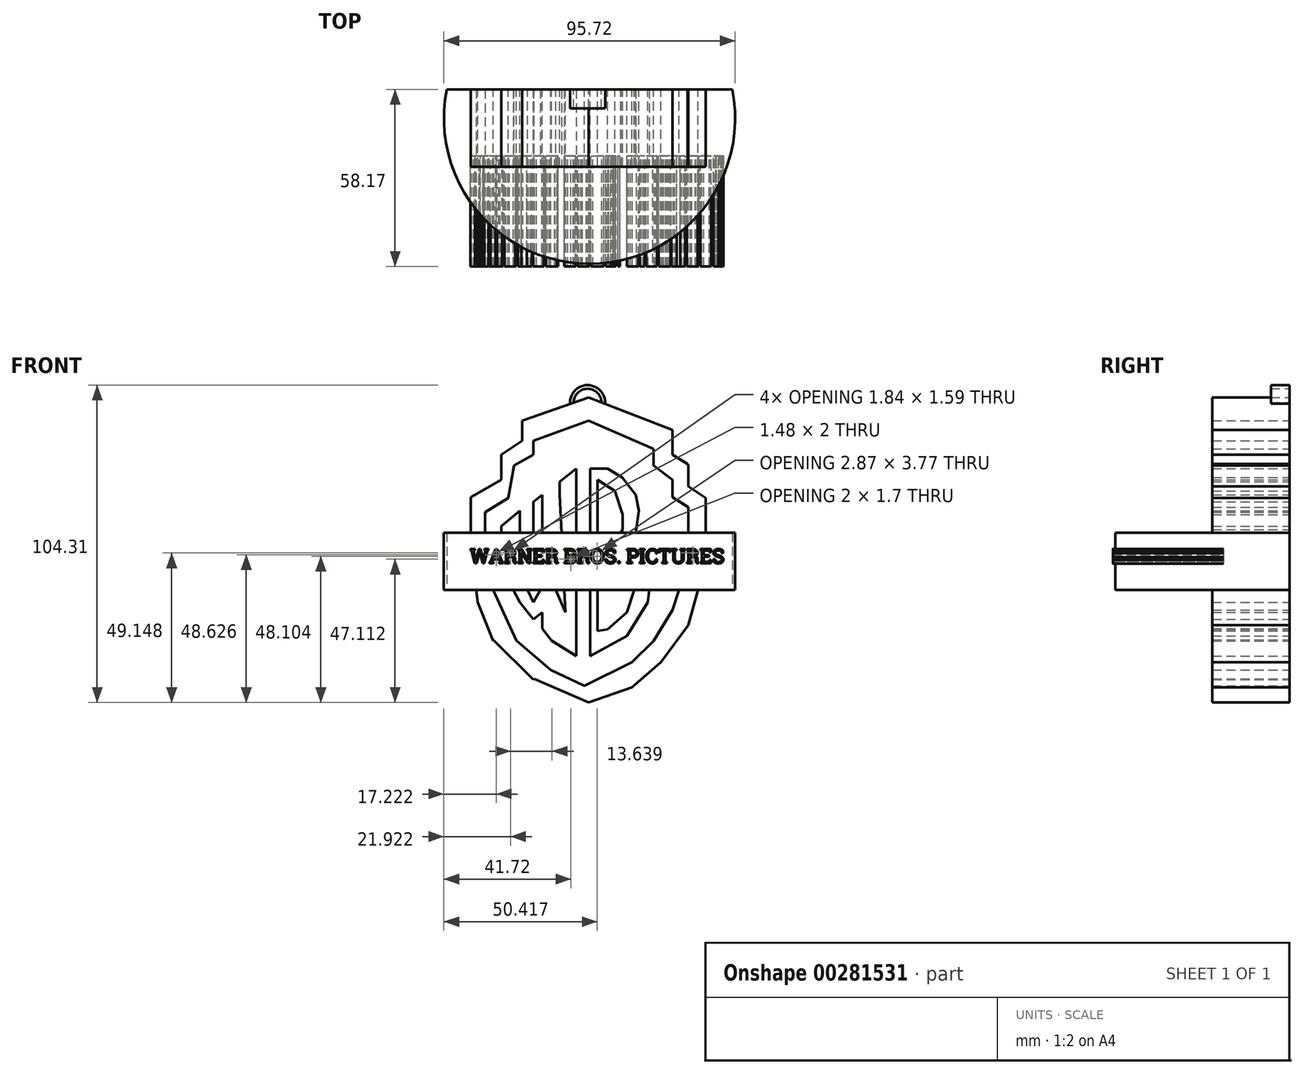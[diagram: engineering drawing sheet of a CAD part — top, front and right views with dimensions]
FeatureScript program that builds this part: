
annotation { "Feature Type Name" : "Feature", "Feature Type Description" : "" }
export const myFeature = defineFeature(function(context is Context, id is Id, definition is map)
    precondition{}
    {
        {
            var Q0;
            Q0=qCreatedBy(makeId("Front.planeOp"),FACE);
            var sketch = newSketch(context, id + "F0", { "sketchPlane" : qUnion([Q0])});
            skLineSegment(sketch, "E0", {"start": v(-31.57, 21) * mm, "end": v(-31.57, 14.04) * mm});
            skLineSegment(sketch, "E1", {"start": v(-31.57, 14.04) * mm, "end": v(-29.37, 3.28) * mm});
            skLineSegment(sketch, "E2", {"start": v(-29.37, 3.28) * mm, "end": v(-25.56, -4) * mm});
            skLineSegment(sketch, "E3", {"start": v(-25.56, -4) * mm, "end": v(-21.1, -9.61) * mm});
            skLineSegment(sketch, "E4", {"start": v(-21.1, -9.61) * mm, "end": v(-18.2, -7.3) * mm});
            skLineSegment(sketch, "E5", {"start": v(-18.2, -7.3) * mm, "end": v(-18.2, -12.73) * mm});
            skLineSegment(sketch, "E6", {"start": v(-18.2, -12.73) * mm, "end": v(-15.13, -16.59) * mm});
            skLineSegment(sketch, "E7", {"start": v(-15.13, -16.59) * mm, "end": v(-6.92, -21.74) * mm});
            skLineSegment(sketch, "E8", {"start": v(-6.92, -21.74) * mm, "end": v(-6.92, 35.57) * mm});
            skLineSegment(sketch, "E9", {"start": v(-6.92, 35.57) * mm, "end": v(-12.38, 31.25) * mm});
            skLineSegment(sketch, "E10", {"start": v(-12.38, 31.25) * mm, "end": v(-10.58, -7.3) * mm});
            skLineSegment(sketch, "E11", {"start": v(-10.58, -7.3) * mm, "end": v(-15.13, 3.28) * mm});
            skLineSegment(sketch, "E12", {"start": v(-15.13, 3.28) * mm, "end": v(-18.2, 18.82) * mm});
            skLineSegment(sketch, "E13", {"start": v(-18.2, 18.82) * mm, "end": v(-18.2, 26.1) * mm});
            skLineSegment(sketch, "E14", {"start": v(-18.2, 26.1) * mm, "end": v(-21.1, 23.8) * mm});
            skLineSegment(sketch, "E15", {"start": v(-21.1, 23.8) * mm, "end": v(-21.1, 18.82) * mm});
            skLineSegment(sketch, "E16", {"start": v(-21.1, 18.82) * mm, "end": v(-18.2, 3.28) * mm});
            skLineSegment(sketch, "E17", {"start": v(-18.2, 3.28) * mm, "end": v(-18.2, 0.92) * mm});
            skLineSegment(sketch, "E18", {"start": v(-21.1, -4.1) * mm, "end": v(-24.53, 3.28) * mm});
            skLineSegment(sketch, "E19", {"start": v(-24.53, 3.28) * mm, "end": v(-25.56, 14.04) * mm});
            skLineSegment(sketch, "E20", {"start": v(-25.56, 14.04) * mm, "end": v(-25.56, 26.1) * mm});
            skLineSegment(sketch, "E21", {"start": v(-25.56, 26.1) * mm, "end": v(-31.57, 21) * mm});
            skLineSegment(sketch, "E22", {"start": v(-18.2, 26.1) * mm, "end": v(-18.2, 31.25) * mm});
            skLineSegment(sketch, "E23", {"start": v(-18.2, 31.25) * mm, "end": v(-21.1, 28.94) * mm});
            skLineSegment(sketch, "E24", {"start": v(-21.1, 28.94) * mm, "end": v(-21.1, 23.8) * mm});
            skLineSegment(sketch, "E25", {"start": v(-12.38, 31.25) * mm, "end": v(-12.38, 35.57) * mm});
            skLineSegment(sketch, "E26", {"start": v(-12.38, 35.57) * mm, "end": v(-6.92, 39.9) * mm});
            skLineSegment(sketch, "E27", {"start": v(-6.92, 39.9) * mm, "end": v(-6.92, 35.57) * mm});
            skLineSegment(sketch, "E28", {"start": v(-2.43, -21.74) * mm, "end": v(-2.43, 39.9) * mm});
            skLineSegment(sketch, "E29", {"start": v(-2.43, 39.9) * mm, "end": v(3.37, 39.9) * mm});
            skLineSegment(sketch, "E30", {"start": v(3.37, 39.9) * mm, "end": v(8.13, 36.9) * mm});
            skLineSegment(sketch, "E31", {"start": v(8.13, 36.9) * mm, "end": v(12.62, 31.25) * mm});
            skLineSegment(sketch, "E32", {"start": v(12.62, 31.25) * mm, "end": v(13.63, 26.1) * mm});
            skLineSegment(sketch, "E33", {"start": v(13.63, 26.1) * mm, "end": v(12.62, 18.82) * mm});
            skLineSegment(sketch, "E34", {"start": v(12.62, 18.82) * mm, "end": v(9.62, 14.04) * mm});
            skLineSegment(sketch, "E35", {"start": v(9.62, 14.04) * mm, "end": v(13.63, 11.52) * mm});
            skLineSegment(sketch, "E36", {"start": v(13.63, 11.52) * mm, "end": v(16.5, 7.9) * mm});
            skLineSegment(sketch, "E37", {"start": v(16.5, 7.9) * mm, "end": v(17.42, 3.28) * mm});
            skLineSegment(sketch, "E38", {"start": v(17.42, 3.28) * mm, "end": v(16.5, -4.1) * mm});
            skLineSegment(sketch, "E39", {"start": v(16.5, -4.1) * mm, "end": v(14.5, -7.3) * mm});
            skLineSegment(sketch, "E40", {"start": v(14.5, -7.3) * mm, "end": v(9.62, -15.06) * mm});
            skLineSegment(sketch, "E41", {"start": v(9.62, -15.06) * mm, "end": v(-2.43, -21.74) * mm});
            skLineSegment(sketch, "E42", {"start": v(0, -13.51) * mm, "end": v(0, 4.3) * mm});
            skLineSegment(sketch, "E43", {"start": v(0, 4.3) * mm, "end": v(3.37, 7.66) * mm});
            skLineSegment(sketch, "E44", {"start": v(3.37, 7.66) * mm, "end": v(7.49, 9.83) * mm});
            skLineSegment(sketch, "E45", {"start": v(7.49, 9.83) * mm, "end": v(12.03, 7.66) * mm});
            skLineSegment(sketch, "E46", {"start": v(12.03, 7.66) * mm, "end": v(12.03, 0) * mm});
            skLineSegment(sketch, "E47", {"start": v(12.03, 0) * mm, "end": v(9.63, -7.3) * mm});
            skLineSegment(sketch, "E48", {"start": v(9.63, -7.3) * mm, "end": v(3.37, -12.98) * mm});
            skLineSegment(sketch, "E49", {"start": v(3.37, -12.98) * mm, "end": v(0, -13.51) * mm});
            skLineSegment(sketch, "E50", {"start": v(0, 9.83) * mm, "end": v(5.75, 15.74) * mm});
            skPoint(sketch, "E50.endSnap0", {"position": v(5.75, 38.4) * mm});
            skLineSegment(sketch, "E51", {"start": v(5.75, 15.74) * mm, "end": v(8.29, 19.78) * mm});
            skLineSegment(sketch, "E52", {"start": v(8.29, 19.78) * mm, "end": v(8.29, 24.78) * mm});
            skLineSegment(sketch, "E53", {"start": v(8.29, 24.78) * mm, "end": v(5.75, 32.55) * mm});
            skLineSegment(sketch, "E54", {"start": v(5.75, 32.55) * mm, "end": v(3.37, 34.05) * mm});
            skLineSegment(sketch, "E55", {"start": v(3.37, 34.05) * mm, "end": v(0, 36.16) * mm});
            skLineSegment(sketch, "E56", {"start": v(0, 36.16) * mm, "end": v(0, 9.83) * mm});
            skLineSegment(sketch, "E57", {"start": v(-15.13, -16.59) * mm, "end": v(-6.92, -13.51) * mm});
            skLineSegment(sketch, "E58", {"start": v(-18.2, -12.73) * mm, "end": v(-10.58, -7.3) * mm});
            skLineSegment(sketch, "E59", {"start": v(-15.13, 3.28) * mm, "end": v(-18.2, 3.28) * mm});
            skLineSegment(sketch, "E60", {"start": v(-21.1, 18.82) * mm, "end": v(-18.2, 18.82) * mm});
            skLineSegment(sketch, "E61", {"start": v(-29.32, 30.24) * mm, "end": v(-36.93, 25.5) * mm});
            skLineSegment(sketch, "E62", {"start": v(-36.93, 25.97) * mm, "end": v(-36.93, 16.94) * mm});
            skLineSegment(sketch, "E63", {"start": v(-36.93, 16.94) * mm, "end": v(-34.31, 0) * mm});
            skLineSegment(sketch, "E64", {"start": v(-34.31, 0) * mm, "end": v(-26.7, -16.57) * mm});
            skLineSegment(sketch, "E65", {"start": v(-26.7, -16.57) * mm, "end": v(-15.3, -26.3) * mm});
            skLineSegment(sketch, "E66", {"start": v(-15.3, -26.3) * mm, "end": v(-4.37, -31.54) * mm});
            skLineSegment(sketch, "E67", {"start": v(-4.37, -31.54) * mm, "end": v(11.31, -23.7) * mm});
            skLineSegment(sketch, "E68", {"start": v(11.31, -23.7) * mm, "end": v(18.44, -16.8) * mm});
            skLineSegment(sketch, "E69", {"start": v(18.44, -16.8) * mm, "end": v(24.62, -6.59) * mm});
            skLineSegment(sketch, "E70", {"start": v(24.62, -6.59) * mm, "end": v(29.84, 9.57) * mm});
            skLineSegment(sketch, "E71", {"start": v(29.84, 9.57) * mm, "end": v(29.84, 21) * mm});
            skLineSegment(sketch, "E72", {"start": v(29.84, 21) * mm, "end": v(29.84, 27.16) * mm});
            skLineSegment(sketch, "E73", {"start": v(29.84, 27.16) * mm, "end": v(24.62, 30.48) * mm});
            skLineSegment(sketch, "E74", {"start": v(24.62, 30.48) * mm, "end": v(24.62, 36.18) * mm});
            skLineSegment(sketch, "E75", {"start": v(24.62, 36.18) * mm, "end": v(18.44, 40.94) * mm});
            skLineSegment(sketch, "E76", {"start": v(18.44, 40.94) * mm, "end": v(18.44, 46.4) * mm});
            skLineSegment(sketch, "E77", {"start": v(18.44, 46.4) * mm, "end": v(-2.95, 55.67) * mm});
            skLineSegment(sketch, "E78", {"start": v(-2.95, 55.67) * mm, "end": v(-21.1, 49.02) * mm});
            skLineSegment(sketch, "E79", {"start": v(-21.1, 49.02) * mm, "end": v(-21.1, 44.5) * mm});
            skLineSegment(sketch, "E80", {"start": v(-21.1, 44.5) * mm, "end": v(-27.42, 40.94) * mm});
            skLineSegment(sketch, "E81", {"start": v(-27.42, 40.94) * mm, "end": v(-29.32, 30.24) * mm});
            skLineSegment(sketch, "E82", {"start": v(-2.95, 63.27) * mm, "end": v(-24.8, 55.67) * mm});
            skLineSegment(sketch, "E83", {"start": v(-24.8, 55.67) * mm, "end": v(-24.8, 49.02) * mm});
            skLineSegment(sketch, "E84", {"start": v(-24.8, 49.02) * mm, "end": v(-31.57, 44.5) * mm});
            skLineSegment(sketch, "E85", {"start": v(-31.57, 44.5) * mm, "end": v(-31.57, 36.18) * mm});
            skLineSegment(sketch, "E86", {"start": v(-31.57, 36.18) * mm, "end": v(-41.68, 30.48) * mm});
            skLineSegment(sketch, "E87", {"start": v(-41.68, 30.48) * mm, "end": v(-41.68, 14.04) * mm});
            skLineSegment(sketch, "E88", {"start": v(-41.92, 13.85) * mm, "end": v(-39.3, -4.1) * mm});
            skLineSegment(sketch, "E89", {"start": v(-39.3, -4.1) * mm, "end": v(-34.31, -16.8) * mm});
            skLineSegment(sketch, "E90", {"start": v(-34.31, -16.33) * mm, "end": v(-21.1, -29.4) * mm});
            skLineSegment(sketch, "E91", {"start": v(-20.77, -29.16) * mm, "end": v(-2.95, -37) * mm});
            skLineSegment(sketch, "E92", {"start": v(-2.95, -37) * mm, "end": v(11.31, -32.01) * mm});
            skLineSegment(sketch, "E93", {"start": v(11.31, -32.01) * mm, "end": v(20.82, -23.7) * mm});
            skLineSegment(sketch, "E94", {"start": v(20.82, -23.7) * mm, "end": v(29.84, -11.58) * mm});
            skLineSegment(sketch, "E95", {"start": v(29.84, -11.58) * mm, "end": v(35.07, 7.67) * mm});
            skLineSegment(sketch, "E96", {"start": v(35.55, 6.96) * mm, "end": v(35.55, 21) * mm});
            skLineSegment(sketch, "E97", {"start": v(35.55, 21) * mm, "end": v(35.55, 30.24) * mm});
            skLineSegment(sketch, "E98", {"start": v(35.55, 30.24) * mm, "end": v(29.84, 34.05) * mm});
            skLineSegment(sketch, "E99", {"start": v(29.84, 34.05) * mm, "end": v(29.84, 40.94) * mm});
            skLineSegment(sketch, "E100", {"start": v(29.6, 41.41) * mm, "end": v(24.62, 44.5) * mm});
            skLineSegment(sketch, "E101", {"start": v(24.62, 44.5) * mm, "end": v(24.62, 52.58) * mm});
            skLineSegment(sketch, "E102", {"start": v(24.62, 52.58) * mm, "end": v(-2.95, 63.27) * mm});
            skLineSegment(sketch, "E103", {"start": v(-21.1, 44.5) * mm, "end": v(-24.8, 49.02) * mm});
            skLineSegment(sketch, "E104", {"start": v(-27.42, 40.94) * mm, "end": v(-31.57, 44.5) * mm});
            skLineSegment(sketch, "E105", {"start": v(-29.32, 30.24) * mm, "end": v(-31.57, 36.18) * mm});
            skLineSegment(sketch, "E106", {"start": v(-36.93, 25.97) * mm, "end": v(-41.68, 30.48) * mm});
            skLineSegment(sketch, "E107", {"start": v(-36.93, 16.94) * mm, "end": v(-41.68, 14.04) * mm});
            skLineSegment(sketch, "E108", {"start": v(-34.31, 0) * mm, "end": v(-39.3, -4.1) * mm});
            skLineSegment(sketch, "E109", {"start": v(-26.7, -16.57) * mm, "end": v(-34.31, -16.33) * mm});
            skLineSegment(sketch, "E110", {"start": v(-15.3, -26.3) * mm, "end": v(-20.77, -29.16) * mm});
            skLineSegment(sketch, "E111", {"start": v(-4.37, -31.54) * mm, "end": v(-2.95, -37) * mm});
            skLineSegment(sketch, "E112", {"start": v(11.31, -23.7) * mm, "end": v(11.31, -32.01) * mm});
            skLineSegment(sketch, "E113", {"start": v(18.44, -16.8) * mm, "end": v(20.82, -23.7) * mm});
            skLineSegment(sketch, "E114", {"start": v(29.84, -11.58) * mm, "end": v(24.62, -6.59) * mm});
            skLineSegment(sketch, "E115", {"start": v(35.55, 6.96) * mm, "end": v(29.84, 9.57) * mm});
            skLineSegment(sketch, "E116", {"start": v(35.55, 21) * mm, "end": v(29.84, 21) * mm});
            skLineSegment(sketch, "E117", {"start": v(29.84, 27.16) * mm, "end": v(35.55, 30.24) * mm});
            skLineSegment(sketch, "E118", {"start": v(29.84, 34.05) * mm, "end": v(24.62, 30.48) * mm});
            skLineSegment(sketch, "E119", {"start": v(29.84, 40.94) * mm, "end": v(24.62, 36.18) * mm});
            skLineSegment(sketch, "E120", {"start": v(24.62, 44.5) * mm, "end": v(18.44, 40.94) * mm});
            skLineSegment(sketch, "E121", {"start": v(18.44, 46.4) * mm, "end": v(24.62, 52.58) * mm});
            skLineSegment(sketch, "E122", {"start": v(-2.95, 55.67) * mm, "end": v(-2.95, 63.27) * mm});
            skLineSegment(sketch, "E123", {"start": v(-34.31, -16.33) * mm, "end": v(-15.3, -26.3) * mm});
            skLineSegment(sketch, "E124", {"start": v(-26.7, -16.57) * mm, "end": v(-20.77, -29.16) * mm});
            skLineSegment(sketch, "E125", {"start": v(-39.3, -4.1) * mm, "end": v(-26.7, -16.57) * mm});
            skLineSegment(sketch, "E126", {"start": v(-34.31, 0) * mm, "end": v(-34.31, -16.33) * mm});
            skLineSegment(sketch, "E127", {"start": v(-41.68, 14.04) * mm, "end": v(-34.31, 0) * mm});
            skLineSegment(sketch, "E128", {"start": v(-36.93, 16.94) * mm, "end": v(-39.3, -4.1) * mm});
            skLineSegment(sketch, "E129", {"start": v(29.84, 40.94) * mm, "end": v(18.44, 40.94) * mm});
            skLineSegment(sketch, "E130", {"start": v(24.62, 36.18) * mm, "end": v(24.62, 44.5) * mm});
            skLineSegment(sketch, "E131", {"start": v(9.62, 14.04) * mm, "end": v(5.75, 15.74) * mm});
            skLineSegment(sketch, "E132", {"start": v(8.29, 19.78) * mm, "end": v(12.62, 18.82) * mm});
            skLineSegment(sketch, "E133", {"start": v(13.63, 26.1) * mm, "end": v(8.29, 24.78) * mm});
            skLineSegment(sketch, "E134", {"start": v(5.75, 32.55) * mm, "end": v(12.62, 31.25) * mm});
            skLineSegment(sketch, "E135", {"start": v(3.37, 34.05) * mm, "end": v(8.13, 36.9) * mm});
            skLineSegment(sketch, "E136", {"start": v(3.37, 39.9) * mm, "end": v(0, 36.16) * mm});
            skLineSegment(sketch, "E137", {"start": v(-2.43, 39.9) * mm, "end": v(0, 36.16) * mm});
            skLineSegment(sketch, "E138", {"start": v(0, 4.3) * mm, "end": v(0, 9.83) * mm});
            skLineSegment(sketch, "E139", {"start": v(3.37, 7.66) * mm, "end": v(5.75, 15.74) * mm});
            skLineSegment(sketch, "E140", {"start": v(7.49, 9.83) * mm, "end": v(9.62, 14.04) * mm});
            skLineSegment(sketch, "E141", {"start": v(12.03, 7.66) * mm, "end": v(13.63, 11.52) * mm});
            skLineSegment(sketch, "E142", {"start": v(16.5, 7.9) * mm, "end": v(12.03, 0) * mm});
            skLineSegment(sketch, "E143", {"start": v(17.42, 3.28) * mm, "end": v(9.63, -7.3) * mm});
            skLineSegment(sketch, "E144", {"start": v(16.5, -4.1) * mm, "end": v(9.63, -7.3) * mm});
            skLineSegment(sketch, "E145", {"start": v(14.5, -7.3) * mm, "end": v(9.63, -7.3) * mm});
            skLineSegment(sketch, "E146", {"start": v(3.37, -12.98) * mm, "end": v(9.62, -15.06) * mm});
            skLineSegment(sketch, "E147", {"start": v(0, -13.51) * mm, "end": v(-2.43, -21.74) * mm});
            skLineSegment(sketch, "E148", {"start": v(-21.1, -4.1) * mm, "end": v(-21.1, -9.61) * mm});
            skLineSegment(sketch, "E149", {"start": v(-18.2, -7.3) * mm, "end": v(-18.2, 0.92) * mm});
            skLineSegment(sketch, "E150", {"start": v(-24.53, 3.28) * mm, "end": v(-25.56, -4) * mm});
            skLineSegment(sketch, "E151", {"start": v(-24.53, 3.28) * mm, "end": v(-29.37, 3.28) * mm});
            skLineSegment(sketch, "E152", {"start": v(-31.57, 14.04) * mm, "end": v(-25.56, 14.04) * mm});
            skLineSegment(sketch, "E153", {"start": v(-34.31, -16.8) * mm, "end": v(-34.31, -16.33) * mm});
            skLineSegment(sketch, "E154", {"start": v(-21.1, -29.4) * mm, "end": v(-20.77, -29.16) * mm});
            skLineSegment(sketch, "E155", {"start": v(-41.92, 13.85) * mm, "end": v(-41.68, 14.04) * mm});
            skLineSegment(sketch, "E156", {"start": v(29.6, 41.41) * mm, "end": v(29.84, 40.94) * mm});
            skLineSegment(sketch, "E157", {"start": v(-18.2, 0.92) * mm, "end": v(-21.1, -4.1) * mm});
            skSolve(sketch);
        }
        {
            var Q0;
            Q0 = qSketchRegion(id + "F0", true);
            var Q1;
            {var subQ0=sQuery(id+"F0.wireOp",EDGE,"E64");Q1=makeQuery(id+"F0.imprint","IMPRINT",FACE,{"disambiguationData":[TD([[makeQuery(id+"F0.imprint","IMPRINT",EDGE,{"derivedFrom":subQ0}),-1.0]])]});}
            var Q2;
            {var subQ0=sQuery(id+"F0.wireOp",EDGE,"E63");Q2=makeQuery(id+"F0.imprint","IMPRINT",FACE,{"disambiguationData":[TD([[makeQuery(id+"F0.imprint","IMPRINT",EDGE,{"derivedFrom":subQ0}),-1.0]])]});}
            var Q3;
            {var subQ0=sQuery(id+"F0.wireOp",EDGE,"E65");Q3=makeQuery(id+"F0.imprint","IMPRINT",FACE,{"disambiguationData":[TD([[makeQuery(id+"F0.imprint","IMPRINT",EDGE,{"derivedFrom":subQ0}),-1.0]])]});}
            var Q4;
            {var subQ0=sQuery(id+"F0.wireOp",EDGE,"E75");Q4=makeQuery(id+"F0.imprint","IMPRINT",FACE,{"disambiguationData":[TD([[makeQuery(id+"F0.imprint","IMPRINT",EDGE,{"derivedFrom":subQ0}),-1.0]])]});}
            var Q5;
            Q5=makeQuery(id+"F0.imprint","IMPRINT",FACE,{"disambiguationData":[TD([[makeQuery(id+"F0.imprint","IMPRINT",EDGE,{"derivedFrom":sQuery(id+"F0.wireOp",EDGE,"E30")}),-1.0]])]});
            var Q6;
            Q6=makeQuery(id+"F0.imprint","IMPRINT",FACE,{"disambiguationData":[TD([[makeQuery(id+"F0.imprint","IMPRINT",EDGE,{"derivedFrom":sQuery(id+"F0.wireOp",EDGE,"E31")}),-1.0]])]});
            var Q7;
            Q7=makeQuery(id+"F0.imprint","IMPRINT",FACE,{"disambiguationData":[TD([[makeQuery(id+"F0.imprint","IMPRINT",EDGE,{"derivedFrom":sQuery(id+"F0.wireOp",EDGE,"E32")}),-1.0]])]});
            var Q8;
            Q8=makeQuery(id+"F0.imprint","IMPRINT",FACE,{"disambiguationData":[TD([[makeQuery(id+"F0.imprint","IMPRINT",EDGE,{"derivedFrom":sQuery(id+"F0.wireOp",EDGE,"E33")}),-1.0]])]});
            var Q9;
            Q9=makeQuery(id+"F0.imprint","IMPRINT",FACE,{"disambiguationData":[TD([[makeQuery(id+"F0.imprint","IMPRINT",EDGE,{"derivedFrom":sQuery(id+"F0.wireOp",EDGE,"E34")}),-1.0]])]});
            var Q10;
            Q10=makeQuery(id+"F0.imprint","IMPRINT",FACE,{"disambiguationData":[TD([[makeQuery(id+"F0.imprint","IMPRINT",EDGE,{"derivedFrom":sQuery(id+"F0.wireOp",EDGE,"E44")}),1.0]])]});
            var Q11;
            Q11=makeQuery(id+"F0.imprint","IMPRINT",FACE,{"disambiguationData":[TD([[makeQuery(id+"F0.imprint","IMPRINT",EDGE,{"derivedFrom":sQuery(id+"F0.wireOp",EDGE,"E43")}),1.0]])]});
            var Q12;
            Q12=makeQuery(id+"F0.imprint","IMPRINT",FACE,{"disambiguationData":[TD([[makeQuery(id+"F0.imprint","IMPRINT",EDGE,{"derivedFrom":sQuery(id+"F0.wireOp",EDGE,"E28")}),-1.0]])]});
            var Q13;
            Q13=makeQuery(id+"F0.imprint","IMPRINT",FACE,{"disambiguationData":[TD([[makeQuery(id+"F0.imprint","IMPRINT",EDGE,{"derivedFrom":sQuery(id+"F0.wireOp",EDGE,"E35")}),-1.0]])]});
            var Q14;
            Q14=makeQuery(id+"F0.imprint","IMPRINT",FACE,{"disambiguationData":[TD([[makeQuery(id+"F0.imprint","IMPRINT",EDGE,{"derivedFrom":sQuery(id+"F0.wireOp",EDGE,"E36")}),-1.0]])]});
            var Q15;
            Q15=makeQuery(id+"F0.imprint","IMPRINT",FACE,{"disambiguationData":[TD([[makeQuery(id+"F0.imprint","IMPRINT",EDGE,{"derivedFrom":sQuery(id+"F0.wireOp",EDGE,"E37")}),-1.0]])]});
            var Q16;
            Q16=makeQuery(id+"F0.imprint","IMPRINT",FACE,{"disambiguationData":[TD([[makeQuery(id+"F0.imprint","IMPRINT",EDGE,{"derivedFrom":sQuery(id+"F0.wireOp",EDGE,"E38")}),-1.0]])]});
            var Q17;
            Q17=makeQuery(id+"F0.imprint","IMPRINT",FACE,{"disambiguationData":[TD([[makeQuery(id+"F0.imprint","IMPRINT",EDGE,{"derivedFrom":sQuery(id+"F0.wireOp",EDGE,"E39")}),-1.0]])]});
            var Q18;
            Q18=makeQuery(id+"F0.imprint","IMPRINT",FACE,{"disambiguationData":[TD([[makeQuery(id+"F0.imprint","IMPRINT",EDGE,{"derivedFrom":sQuery(id+"F0.wireOp",EDGE,"E40")}),-1.0]])]});
            var Q19;
            Q19=makeQuery(id+"F0.imprint","IMPRINT",FACE,{"disambiguationData":[TD([[makeQuery(id+"F0.imprint","IMPRINT",EDGE,{"derivedFrom":sQuery(id+"F0.wireOp",EDGE,"E41")}),-1.0]])]});
            var Q20;
            Q20=makeQuery(id+"F0.imprint","IMPRINT",FACE,{"disambiguationData":[TD([[makeQuery(id+"F0.imprint","IMPRINT",EDGE,{"derivedFrom":sQuery(id+"F0.wireOp",EDGE,"E29")}),-1.0]])]});
            var Q21;
            Q21=makeQuery(id+"F0.imprint","IMPRINT",FACE,{"disambiguationData":[TD([[makeQuery(id+"F0.imprint","IMPRINT",EDGE,{"derivedFrom":sQuery(id+"F0.wireOp",EDGE,"E9")}),-1.0]])]});
            var Q22;
            Q22=makeQuery(id+"F0.imprint","IMPRINT",FACE,{"disambiguationData":[TD([[makeQuery(id+"F0.imprint","IMPRINT",EDGE,{"derivedFrom":sQuery(id+"F0.wireOp",EDGE,"E6")}),1.0]])]});
            var Q23;
            {var subQ0=sQuery(id+"F0.wireOp",EDGE,"E7");Q23=makeQuery(id+"F0.imprint","IMPRINT",FACE,{"disambiguationData":[TD([[makeQuery(id+"F0.imprint","IMPRINT",EDGE,{"derivedFrom":subQ0}),1.0]])]});}
            var Q24;
            Q24=makeQuery(id+"F0.imprint","IMPRINT",FACE,{"disambiguationData":[TD([[makeQuery(id+"F0.imprint","IMPRINT",EDGE,{"derivedFrom":sQuery(id+"F0.wireOp",EDGE,"E5")}),1.0]])]});
            var Q25;
            Q25=makeQuery(id+"F0.imprint","IMPRINT",FACE,{"disambiguationData":[TD([[makeQuery(id+"F0.imprint","IMPRINT",EDGE,{"derivedFrom":sQuery(id+"F0.wireOp",EDGE,"E12")}),1.0]])]});
            var Q26;
            Q26=makeQuery(id+"F0.imprint","IMPRINT",FACE,{"disambiguationData":[TD([[makeQuery(id+"F0.imprint","IMPRINT",EDGE,{"derivedFrom":sQuery(id+"F0.wireOp",EDGE,"E13")}),1.0]])]});
            var Q27;
            Q27=makeQuery(id+"F0.imprint","IMPRINT",FACE,{"disambiguationData":[TD([[makeQuery(id+"F0.imprint","IMPRINT",EDGE,{"derivedFrom":sQuery(id+"F0.wireOp",EDGE,"E14")}),-1.0]])]});
            var Q28;
            Q28=makeQuery(id+"F0.imprint","IMPRINT",FACE,{"disambiguationData":[TD([[makeQuery(id+"F0.imprint","IMPRINT",EDGE,{"derivedFrom":sQuery(id+"F0.wireOp",EDGE,"E0")}),1.0]])]});
            var Q29;
            Q29=makeQuery(id+"F0.imprint","IMPRINT",FACE,{"disambiguationData":[TD([[makeQuery(id+"F0.imprint","IMPRINT",EDGE,{"derivedFrom":sQuery(id+"F0.wireOp",EDGE,"E1")}),1.0]])]});
            var Q30;
            Q30=makeQuery(id+"F0.imprint","IMPRINT",FACE,{"disambiguationData":[TD([[makeQuery(id+"F0.imprint","IMPRINT",EDGE,{"derivedFrom":sQuery(id+"F0.wireOp",EDGE,"E2")}),1.0]])]});
            var Q31;
            Q31=makeQuery(id+"F0.imprint","IMPRINT",FACE,{"disambiguationData":[TD([[makeQuery(id+"F0.imprint","IMPRINT",EDGE,{"derivedFrom":sQuery(id+"F0.wireOp",EDGE,"E3")}),1.0]])]});
            var Q32;
            Q32=makeQuery(id+"F0.imprint","IMPRINT",FACE,{"disambiguationData":[TD([[makeQuery(id+"F0.imprint","IMPRINT",EDGE,{"derivedFrom":sQuery(id+"F0.wireOp",EDGE,"E4")}),1.0]])]});
            extrude(context, id + "F1", {"entities" : qUnion([Q0, Q1, Q2, Q3, Q4, Q5, Q6, Q7, Q8, Q9, Q10, Q11, Q12, Q13, Q14, Q15, Q16, Q17, Q18, Q19, Q20, Q21, Q22, Q23, Q24, Q25, Q26, Q27, Q28, Q29, Q30, Q31, Q32]), "depth" : 25.4 * mm});
        }
        {
            var Q0;
            Q0=qCreatedBy(makeId("Top.planeOp"),FACE);
            var sketch = newSketch(context, id + "F2", { "sketchPlane" : qUnion([Q0])});
            skArc(sketch, "E158", {"start": v(-49.54, 0) * mm, "mid": v(-2.62, -57.33) * mm, "end": v(44.3, 0) * mm});
            skArc(sketch, "E159", {"start": v(-43.66, 0) * mm, "mid": v(-2.62, -51.6) * mm, "end": v(38.42, 0) * mm});
            skLineSegment(sketch, "E160", {"start": v(-49.54, 0) * mm, "end": v(44.3, 0) * mm});
            skSolve(sketch);
        }
        {
            var Q0;
            Q0 = qSketchRegion(id + "F2", true);
            extrude(context, id + "F3", {"entities" : qUnion([Q0]), "operationType" : NewBodyOperationType.ADD, "depth" : 18.8 * mm});
        }
        {
            var Q0;
            Q0=qCreatedBy(makeId("Front.planeOp"),FACE);
            var sketch = newSketch(context, id + "F4", { "sketchPlane" : qUnion([Q0])});
            skText(sketch, "E161", { "text": "WARNER BROS. PICTURES\n", "fontName": "RobotoSlab-Regular.ttf"});
            const initialGuessF4  = {"E161": [-0.0418, 0.00877, 1, 0, 0.00473]};
            skSetInitialGuess(sketch, initialGuessF4);
            skSolve(sketch);
        }
        {
            var Q0;
            Q0 = qSketchRegion(id + "F4", true);
            extrude(context, id + "F5", {"entities" : qUnion([Q0]), "depth" : 58.17 * mm, "hasSecondDirection" : true, "secondDirectionOppositeDirection" : false, "secondDirectionDepth" : 21.84 * mm});
        }
        {
            var Q0;
            Q0=qCreatedBy(makeId("Front.planeOp"),FACE);
            var sketch = newSketch(context, id + "F6", { "sketchPlane" : qUnion([Q0])});
            skCircle(sketch, "E162", {"center": v(-3.26, 61.55) * mm, "radius": 5.76 * mm});
            skCircle(sketch, "E163", {"center": v(-3.26, 61.55) * mm, "radius": 4.57 * mm});
            skSolve(sketch);
        }
        {
            var Q0;
            Q0 = qSketchRegion(id + "F6", true);
            extrude(context, id + "F7", {"entities" : qUnion([Q0]), "operationType" : NewBodyOperationType.ADD, "depth" : 6.22 * mm});
        }
    });
